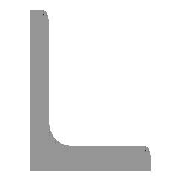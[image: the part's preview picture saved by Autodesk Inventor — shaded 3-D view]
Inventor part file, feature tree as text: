
AUTODESK INVENTOR PART (.ipt)
format: ipt  version: 2013 (Build 170138000, 138)  size: 150,528 bytes
history: native  units: mm (DEFAULTED — no unit token found)
features: plane x7, other x4, sketch x4, extrude x2
ambient origin geometry x8: Origin, YZ Plane, XZ Plane, XY Plane, X Axis, Y Axis, Z Axis, Center Point
bodies: Solid1 (feature_tree), Body (feature_tree)
feature tree (17):
  parser-record x1  (decoder bookkeeping rows leaked as tree rows — omitted from the tree; the rows remain in map.json)
  other  "Driven Length"
  other  "Start plane"
  other  "End plane"
  plane  "Work Plane4"
  plane  "Work Plane5"
  plane  "Work Plane6"
  extrude  "Extrusion2"  Depth=38.1mm
  plane  "Work Plane7"
  plane  "Work Plane8"
  plane  "Work Plane9"
  extrude  "Extrusion3"  Depth=4.7625mm
  sketch  "Sketch3"  dims[d0=38.1mm d1=38.1mm]
  plane  "Work Plane3"
  sketch  "Sketch4"  dims[d2=4.7625mm d3=4.7625mm]
  sketch  "Sketch5"  dims[d4=561.975mm]
  sketch  "Sketch6"  dims[d5=0.0mm d10=0.0mm d11=0.0mm d12=-0.0mm d13=561.975mm d14=4.826mm d15=2.286mm d16=90.0deg d17=561.975mm d18=3.302mm d19=0.0mm d20=3.302mm d21=0.0mm]
